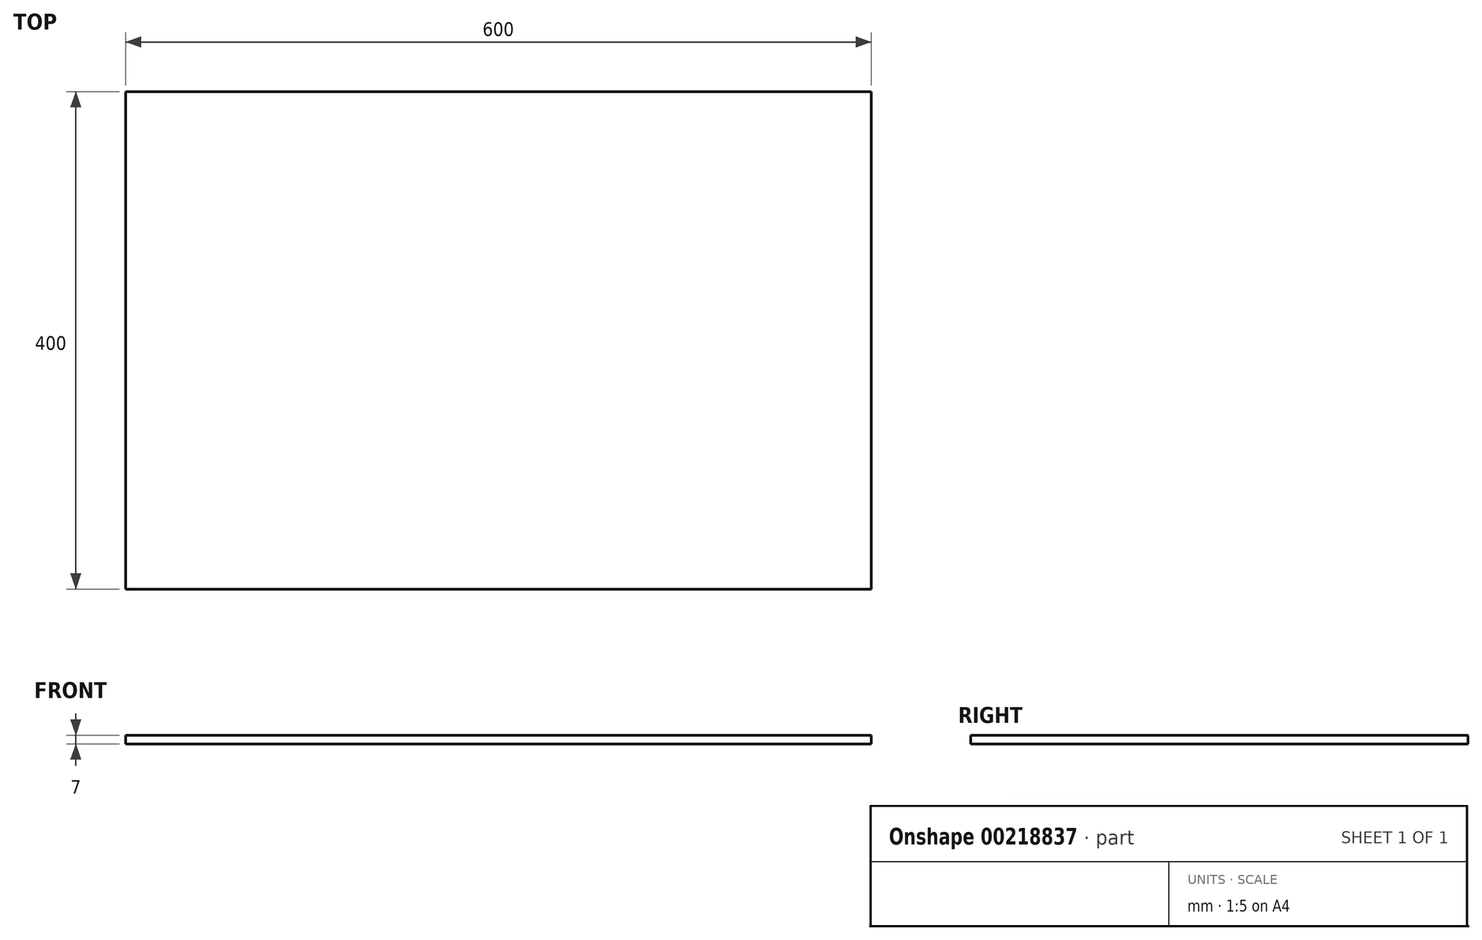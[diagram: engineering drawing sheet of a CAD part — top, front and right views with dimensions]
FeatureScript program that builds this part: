
annotation { "Feature Type Name" : "Feature", "Feature Type Description" : "" }
export const myFeature = defineFeature(function(context is Context, id is Id, definition is map)
    precondition{}
    {
        {
            var Q0;
            Q0=qCreatedBy(makeId("Top.planeOp"),FACE);
            var sketch = newSketch(context, id + "F0", { "sketchPlane" : qUnion([Q0])});
            skLineSegment(sketch, "E0.bottom", {"start": v(300, -200) * mm, "end": v(-300, -200) * mm});
            skLineSegment(sketch, "E0.top", {"start": v(300, 200) * mm, "end": v(-300, 200) * mm});
            skLineSegment(sketch, "E0.left", {"start": v(300, -200) * mm, "end": v(300, 200) * mm});
            skLineSegment(sketch, "E0.right", {"start": v(-300, -200) * mm, "end": v(-300, 200) * mm});
            skPoint(sketch, "E0.middle", {"position": v(0, 0) * mm});
            skSolve(sketch);
        }
        {
            var Q0;
            Q0=makeQuery(id+"F0.imprint","IMPRINT",FACE,{"disambiguationData":[TD([[makeQuery(id+"F0.imprint","IMPRINT",EDGE,{"derivedFrom":sQuery(id+"F0.wireOp",EDGE,"E0.bottom")}),-1.0]])]});
            extrude(context, id + "F1", {"entities" : qUnion([Q0]), "depth" : 7 * mm});
        }
    });
